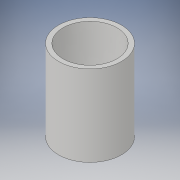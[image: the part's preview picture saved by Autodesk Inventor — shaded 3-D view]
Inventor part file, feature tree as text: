
AUTODESK INVENTOR PART (.ipt)
format: ipt  version: 2019 (Build 230136000, 136)  size: 95,744 bytes
history: native  units: mm
features: extrude x1, sketch x1
ambient origin geometry x8: Origin, YZ Plane, XZ Plane, XY Plane, X Axis, Y Axis, Z Axis, Center Point
bodies: Solid1 (feature_tree)
feature tree (2):
  extrude  "Extrusion1"  Depth=9.0mm
  sketch  "Sketch1"  dims[d0=7.0mm d1=6.0mm d2=9.0mm d3=0.0mm]
